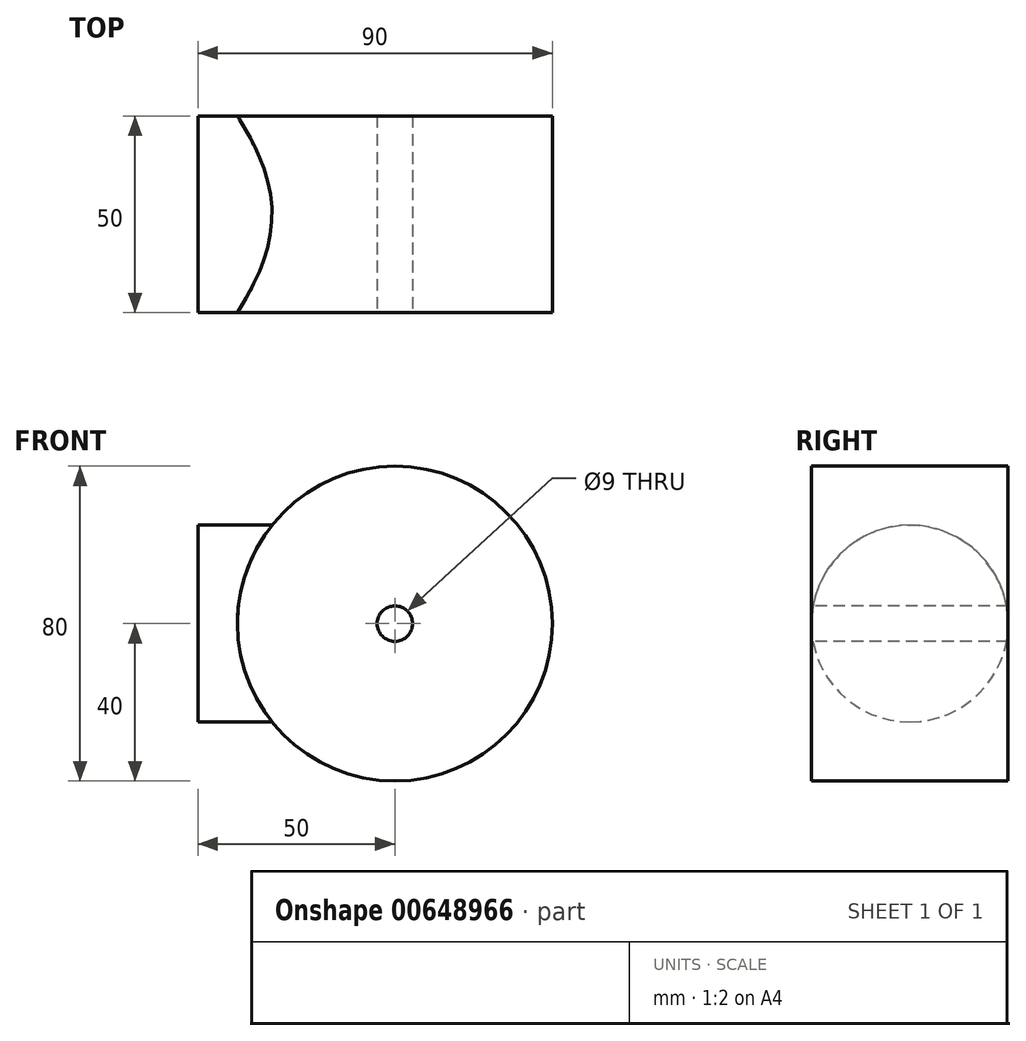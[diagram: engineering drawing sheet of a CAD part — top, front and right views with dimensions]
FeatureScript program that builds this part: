
annotation { "Feature Type Name" : "Feature", "Feature Type Description" : "" }
export const myFeature = defineFeature(function(context is Context, id is Id, definition is map)
    precondition{}
    {
        {
            var Q0;
            Q0=qCreatedBy(makeId("Front.planeOp"),FACE);
            var sketch = newSketch(context, id + "F0", { "sketchPlane" : qUnion([Q0])});
            skCircle(sketch, "E0", {"center": v(0, 0) * mm, "radius": 40 * mm});
            skSolve(sketch);
        }
        {
            var Q0;
            Q0 = qSketchRegion(id + "F0", true);
            extrude(context, id + "F1", {"entities" : qUnion([Q0]), "endBound" : BoundingType.SYMMETRIC, "depth" : 50 * mm, "offsetDistance" : 25 * mm});
        }
        {
            var Q0;
            Q0=qCreatedBy(makeId("Right.planeOp"),FACE);
            cPlane(context, id + "F2", {"entities" : qUnion([Q0]), "cplaneType" : CPlaneType.OFFSET, "offset" : 50 * mm, "oppositeDirection" : true, "width" : 150 * mm, "height" : 150 * mm});
        }
        {
            var Q0;
            Q0=qCreatedBy(id+"F2.planeOp",FACE);
            var sketch = newSketch(context, id + "F3", { "sketchPlane" : qUnion([Q0])});
            skCircle(sketch, "E1", {"center": v(0, 0) * mm, "radius": 25 * mm});
            skSolve(sketch);
        }
        {
            var Q0;
            Q0 = qSketchRegion(id + "F3", true);
            var Q1;
            Q1=makeQuery(id+"F1.opExtrude","SWEPT_FACE",FACE,{"disambiguationData":[OSD([sQuery(id+"F0.wireOp",EDGE,"E0")])]});
            extrude(context, id + "F4", {"entities" : qUnion([Q0]), "operationType" : NewBodyOperationType.ADD, "endBound" : BoundingType.UP_TO_SURFACE, "depth" : 25 * mm, "endBoundEntityFace" : qUnion([Q1]), "offsetDistance" : 25 * mm});
        }
        {
            var Q0;
            Q0=makeQuery(id+"F1.opExtrude","CAP_FACE",FACE,{"disambiguationData":[OSD([sQuery(id+"F0.wireOp",EDGE,"E0")])],"isStart":false});
            var sketch = newSketch(context, id + "F5", { "sketchPlane" : qUnion([Q0])});
            skCircle(sketch, "E2", {"center": v(0, 0) * mm, "radius": 4.5 * mm});
            skSolve(sketch);
        }
        {
            var Q0;
            Q0 = qSketchRegion(id + "F5", true);
            extrude(context, id + "F6", {"entities" : qUnion([Q0]), "operationType" : NewBodyOperationType.REMOVE, "endBound" : BoundingType.THROUGH_ALL, "oppositeDirection" : true, "depth" : 25 * mm, "offsetDistance" : 25 * mm});
        }
    });
